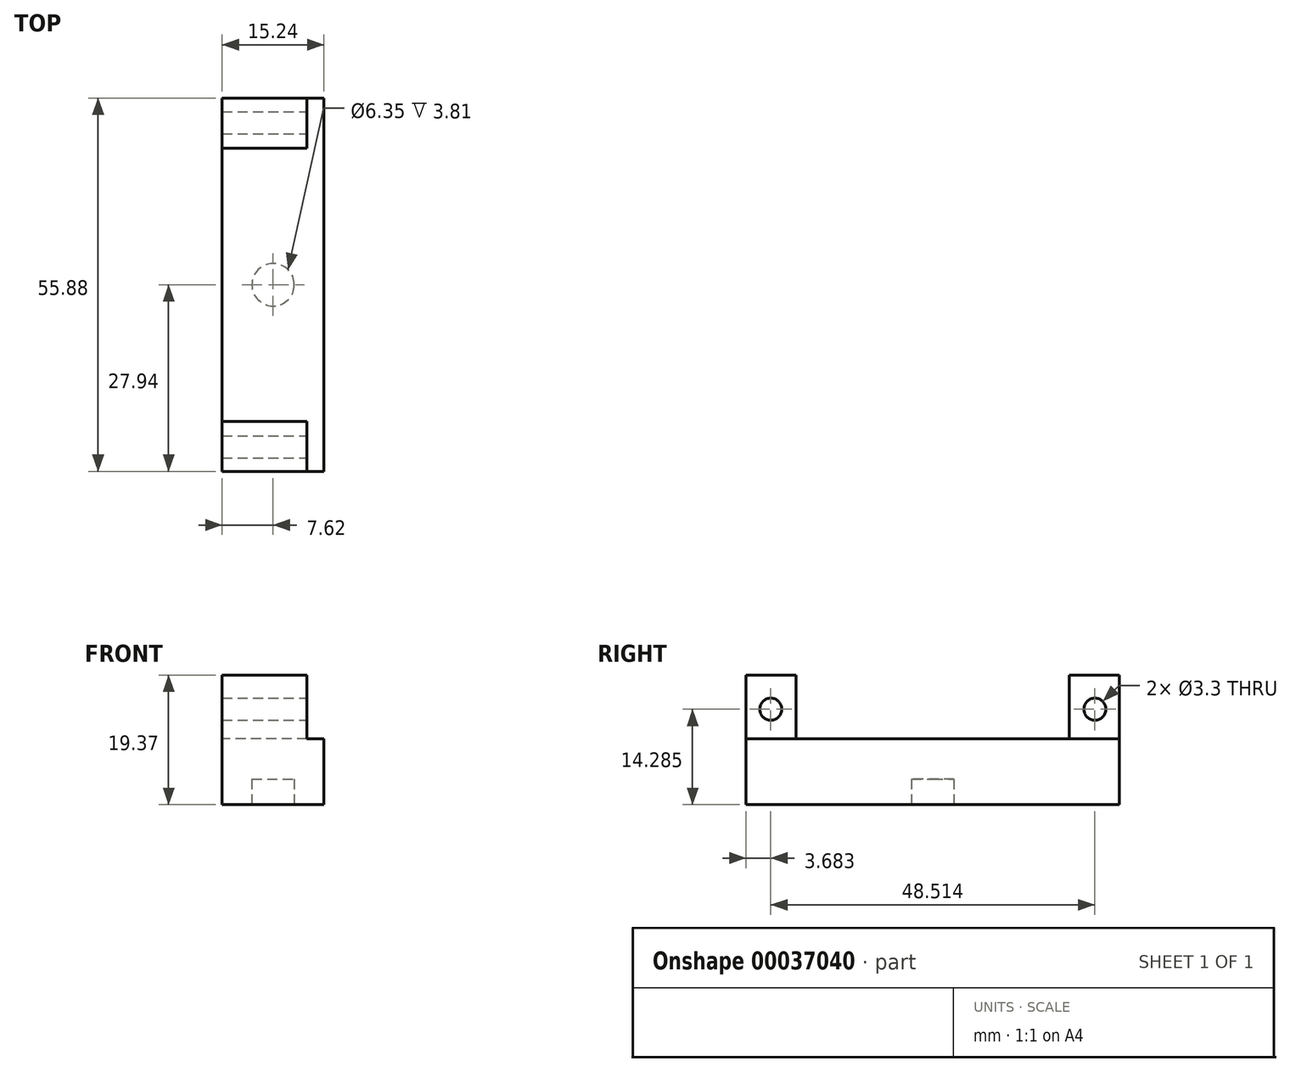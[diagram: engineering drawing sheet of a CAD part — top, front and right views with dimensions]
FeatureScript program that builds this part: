
annotation { "Feature Type Name" : "Feature", "Feature Type Description" : "" }
export const myFeature = defineFeature(function(context is Context, id is Id, definition is map)
    precondition{}
    {
        {
            var Q0;
            Q0=qCreatedBy(makeId("Right.planeOp"),FACE);
            var sketch = newSketch(context, id + "F0", { "sketchPlane" : qUnion([Q0])});
            skLineSegment(sketch, "E0", {"start": v(0, -9.84) * mm, "end": v(27.94, -9.84) * mm});
            skLineSegment(sketch, "E1", {"start": v(27.94, -9.84) * mm, "end": v(27.94, 9.53) * mm});
            skLineSegment(sketch, "E2", {"start": v(27.94, 9.53) * mm, "end": v(20.45, 9.53) * mm});
            skLineSegment(sketch, "E3", {"start": v(20.45, 9.53) * mm, "end": v(20.45, 0) * mm});
            skLineSegment(sketch, "E4", {"start": v(20.45, 0) * mm, "end": v(0, 0) * mm});
            skLineSegment(sketch, "E5", {"start": v(0, 0) * mm, "end": v(0, -9.84) * mm});
            skSolve(sketch);
        }
        {
            var Q0;
            Q0=qSketchRegion(id+"F0",true);
            extrude(context, id + "F1", {"entities" : qUnion([Q0]), "endBound" : BoundingType.SYMMETRIC, "depth" : 15.24 * mm});
        }
        {
            var Q0;
            Q0=makeQuery(id+"F1.opExtrude","SWEPT_BODY",BODY,{"disambiguationData":[OSD([sQuery(id+"F0.wireOp",EDGE,"E0"),sQuery(id+"F0.wireOp",EDGE,"E1"),sQuery(id+"F0.wireOp",EDGE,"E2"),sQuery(id+"F0.wireOp",EDGE,"E3"),sQuery(id+"F0.wireOp",EDGE,"E4"),sQuery(id+"F0.wireOp",EDGE,"E5")])]});
            var Q1;
            Q1=qCreatedBy(makeId("Front.planeOp"),FACE);
            mirror(context, id + "F2", {"operationType" : NewBodyOperationType.ADD, "entities" : qUnion([Q0]), "mirrorPlane" : qUnion([Q1])});
        }
        {
            var Q0;
            {var subQ0=makeQuery(id+"F1.opExtrude","CAP_FACE",FACE,{"disambiguationData":[OSD([sQuery(id+"F0.wireOp",EDGE,"E0"),sQuery(id+"F0.wireOp",EDGE,"E1"),sQuery(id+"F0.wireOp",EDGE,"E2"),sQuery(id+"F0.wireOp",EDGE,"E3"),sQuery(id+"F0.wireOp",EDGE,"E4"),sQuery(id+"F0.wireOp",EDGE,"E5")])],"isStart":false});Q0=makeQuery(id+"F2.boolean.opBoolean","MERGE",FACE,{"derivedFrom":[subQ0,makeQuery(id+"F2.opPattern","COPY",FACE,{"derivedFrom":subQ0,"instanceName":"1"})]});}
            var sketch = newSketch(context, id + "F3", { "sketchPlane" : qUnion([Q0])});
            skCircle(sketch, "E6", {"center": v(-24.26, 4.44) * mm, "radius": 1.65 * mm});
            skCircle(sketch, "E7", {"center": v(24.26, 4.45) * mm, "radius": 1.65 * mm});
            skLineSegment(sketch, "E8", {"start": v(24.26, 4.45) * mm, "end": v(-24.26, 4.44) * mm, "construction": true});
            skSolve(sketch);
        }
        {
            var Q0;
            Q0=qSketchRegion(id+"F3",true);
            extrude(context, id + "F4", {"entities" : qUnion([Q0]), "operationType" : NewBodyOperationType.REMOVE, "oppositeDirection" : true, "depth" : 25.4 * mm});
        }
        {
            var Q0;
            {var subQ0=makeQuery(id+"F1.opExtrude","SWEPT_FACE",FACE,{"disambiguationData":[OSD([sQuery(id+"F0.wireOp",EDGE,"E0")])]});Q0=makeQuery(id+"F2.boolean.opBoolean","MERGE",FACE,{"derivedFrom":[subQ0,makeQuery(id+"F2.opPattern","COPY",FACE,{"derivedFrom":subQ0,"instanceName":"1"})]});}
            var sketch = newSketch(context, id + "F5", { "sketchPlane" : qUnion([Q0])});
            skPoint(sketch, "E9", {"position": v(0, 0) * mm});
            skCircle(sketch, "E10", {"center": v(0, 0) * mm, "radius": 3.18 * mm});
            skSolve(sketch);
        }
        {
            var Q0;
            Q0=makeQuery(id+"F5.imprint","IMPRINT",FACE,{"disambiguationData":[TD([[makeQuery(id+"F5.imprint","IMPRINT",EDGE,{"derivedFrom":sQuery(id+"F5.wireOp",EDGE,"E10")}),1.0]])]});
            extrude(context, id + "F6", {"entities" : qUnion([Q0]), "operationType" : NewBodyOperationType.REMOVE, "oppositeDirection" : true, "depth" : 3.8 * mm});
        }
        {
            var Q0;
            {var subQ0=makeQuery(id+"F1.opExtrude","CAP_FACE",FACE,{"disambiguationData":[OSD([sQuery(id+"F0.wireOp",EDGE,"E0"),sQuery(id+"F0.wireOp",EDGE,"E1"),sQuery(id+"F0.wireOp",EDGE,"E2"),sQuery(id+"F0.wireOp",EDGE,"E3"),sQuery(id+"F0.wireOp",EDGE,"E4"),sQuery(id+"F0.wireOp",EDGE,"E5")])],"isStart":false});Q0=makeQuery(id+"F2.boolean.opBoolean","MERGE",FACE,{"derivedFrom":[subQ0,makeQuery(id+"F2.opPattern","COPY",FACE,{"derivedFrom":subQ0,"instanceName":"1"})]});}
            var sketch = newSketch(context, id + "F7", { "sketchPlane" : qUnion([Q0])});
            skLineSegment(sketch, "E11.bottom", {"start": v(-27.94, 9.53) * mm, "end": v(27.94, 9.53) * mm});
            skLineSegment(sketch, "E11.top", {"start": v(-27.94, 0) * mm, "end": v(27.94, 0) * mm});
            skLineSegment(sketch, "E11.left", {"start": v(-27.94, 9.53) * mm, "end": v(-27.94, 0) * mm});
            skLineSegment(sketch, "E11.right", {"start": v(27.94, 9.53) * mm, "end": v(27.94, 0) * mm});
            skSolve(sketch);
        }
        {
            var Q0;
            Q0 = qSketchRegion(id + "F7", true);
            extrude(context, id + "F8", {"entities" : qUnion([Q0]), "operationType" : NewBodyOperationType.REMOVE, "oppositeDirection" : true, "depth" : 2.54 * mm});
        }
    });
